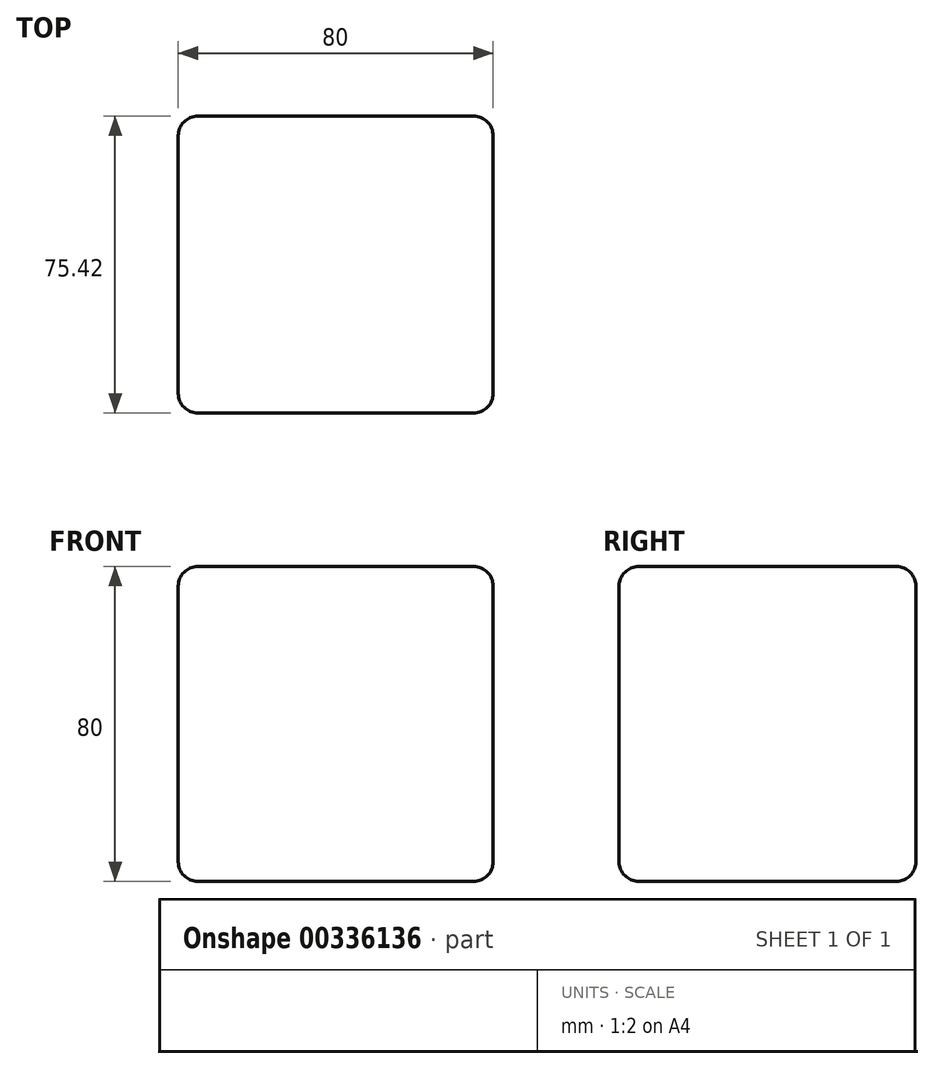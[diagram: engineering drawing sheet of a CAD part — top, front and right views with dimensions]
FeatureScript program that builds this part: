
annotation { "Feature Type Name" : "Feature", "Feature Type Description" : "" }
export const myFeature = defineFeature(function(context is Context, id is Id, definition is map)
    precondition{}
    {
        {
            var Q0;
            Q0=qCreatedBy(makeId("Top.planeOp"),FACE);
            var sketch = newSketch(context, id + "F0", { "sketchPlane" : qUnion([Q0])});
            skLineSegment(sketch, "E0.bottom", {"start": v(40, -37.71) * mm, "end": v(-40, -37.71) * mm});
            skLineSegment(sketch, "E0.top", {"start": v(40, 37.71) * mm, "end": v(-40, 37.71) * mm});
            skLineSegment(sketch, "E0.left", {"start": v(40, -37.71) * mm, "end": v(40, 37.71) * mm});
            skLineSegment(sketch, "E0.right", {"start": v(-40, -37.71) * mm, "end": v(-40, 37.71) * mm});
            skPoint(sketch, "E0.middle", {"position": v(0, 0) * mm});
            skSolve(sketch);
        }
        {
            var Q0;
            Q0=makeQuery(id+"F0.imprint","IMPRINT",FACE,{"disambiguationData":[TD([[makeQuery(id+"F0.imprint","IMPRINT",EDGE,{"derivedFrom":sQuery(id+"F0.wireOp",EDGE,"E0.bottom")}),-1.0]])]});
            extrude(context, id + "F1", {"entities" : qUnion([Q0]), "endBound" : BoundingType.SYMMETRIC, "depth" : 80 * mm});
        }
        {
            var Q0;
            Q0=makeQuery(id+"F1.opExtrude","CAP_FACE",FACE,{"disambiguationData":[OSD([sQuery(id+"F0.wireOp",EDGE,"E0.bottom"),sQuery(id+"F0.wireOp",EDGE,"E0.top"),sQuery(id+"F0.wireOp",EDGE,"E0.left"),sQuery(id+"F0.wireOp",EDGE,"E0.right")])],"isStart":false});
            var Q1;
            Q1=makeQuery(id+"F1.opExtrude","SWEPT_FACE",FACE,{"disambiguationData":[OSD([sQuery(id+"F0.wireOp",EDGE,"E0.left")])]});
            var Q2;
            Q2=makeQuery(id+"F1.opExtrude","SWEPT_FACE",FACE,{"disambiguationData":[OSD([sQuery(id+"F0.wireOp",EDGE,"E0.right")])]});
            var Q3;
            Q3=makeQuery(id+"F1.opExtrude","CAP_FACE",FACE,{"disambiguationData":[OSD([sQuery(id+"F0.wireOp",EDGE,"E0.bottom"),sQuery(id+"F0.wireOp",EDGE,"E0.top"),sQuery(id+"F0.wireOp",EDGE,"E0.left"),sQuery(id+"F0.wireOp",EDGE,"E0.right")])],"isStart":true});
            fillet(context, id + "F2", {"entities" : qUnion([Q0, Q1, Q2, Q3]), "radius" : 5 * mm, "tangentPropagation" : true, "allowEdgeOverflow" : false});
        }
    });
